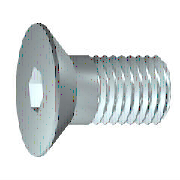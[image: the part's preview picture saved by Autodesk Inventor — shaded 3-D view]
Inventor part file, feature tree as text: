
AUTODESK INVENTOR PART (.ipt)
format: ipt  version: 2024.2 (Build 282272000, 272)  size: 182,784 bytes
history: native  units: mm (DEFAULTED — no unit token found)
features: extrude x1, plane x1
ambient origin geometry x7: Origin, YZ Plane, XY Plane, X Axis, Y Axis, Z Axis, Center Point
bodies: Solid1 (feature_tree), Body (feature_tree)
feature tree (2):
  extrude  "Slot"  Depth=22.0mm
  plane  "Work Plane1"
